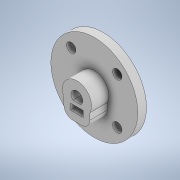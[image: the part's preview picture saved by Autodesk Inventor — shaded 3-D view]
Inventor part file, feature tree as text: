
AUTODESK INVENTOR PART (.ipt)
format: ipt  version: 2020 (Build 240168000, 168)  size: 188,928 bytes
history: native  units: mm
features: sketch x9, extrude x6, fillet x2, other x1
ambient origin geometry x8: Origin, YZ Plane, XZ Plane, XY Plane, X Axis, Y Axis, Z Axis, Center Point
bodies: Body1 (feature_tree)
feature tree (18):
  other  "Bryła1"
  extrude  "Wyciągnięcie proste1"  Depth=40.0mm
  extrude  "Wyciągnięcie proste2"  Depth=4.3mm
  sketch  "Szkic3"
  sketch  "Szkic4"
  sketch  "Szkic5"
  extrude  "Wyciągnięcie proste3"  Depth=40.0mm TaperAngle=360.0deg
  extrude  "Wyciągnięcie proste4"  Depth=5.36mm
  extrude  "Wyciągnięcie proste5"  Depth=4.0mm TaperAngle=0.0deg
  sketch  "Szkic7"
  extrude  "Wyciągnięcie proste6"  Depth=13.4mm
  fillet  "Zaokrąglenie1"  Radius=6.0mm
  fillet  "Zaokrąglenie2"  Radius=7.0mm
  sketch  "Szkic9"
  sketch  "Szkic1"
  sketch  "Szkic2"
  sketch  "Szkic6"
  sketch  "Szkic8"
